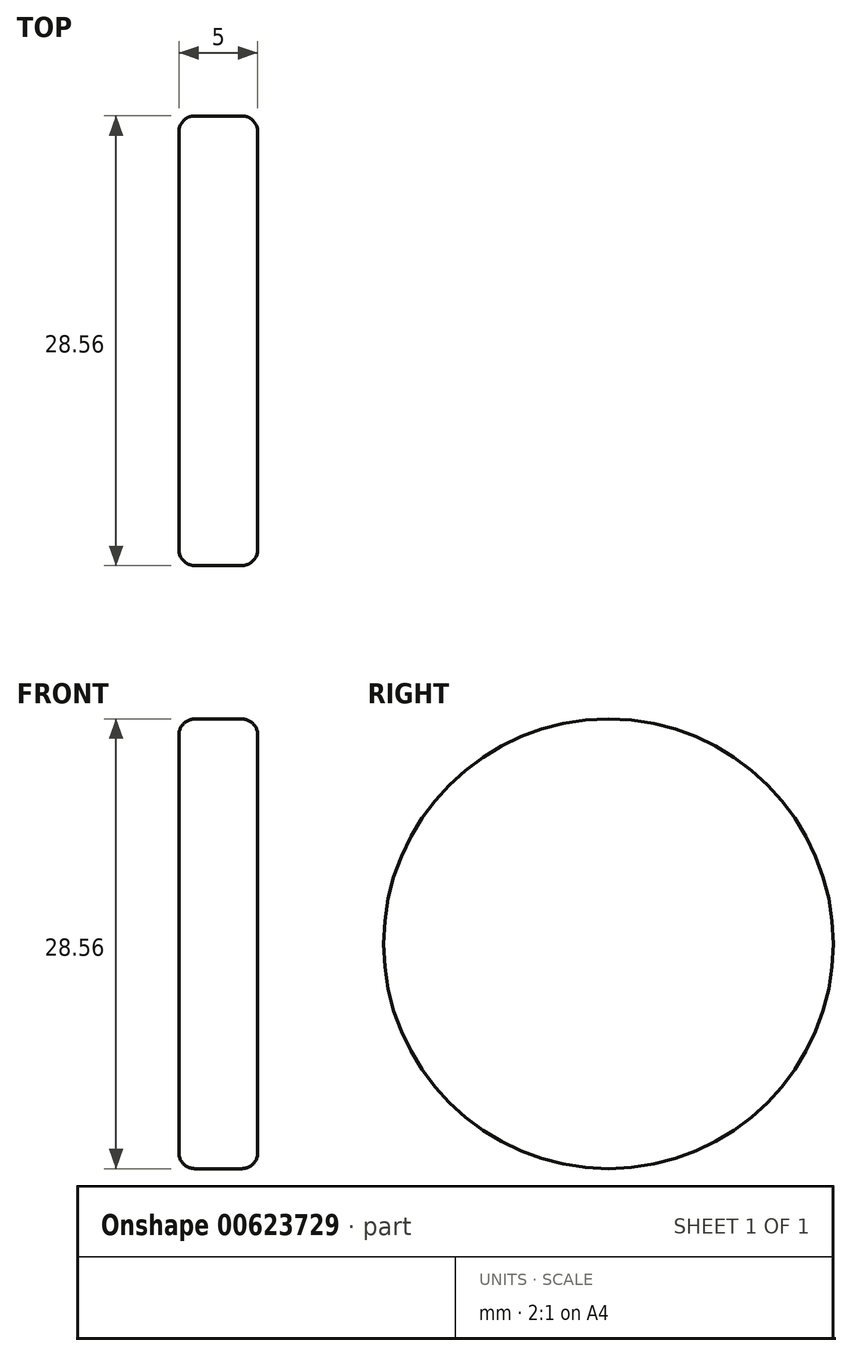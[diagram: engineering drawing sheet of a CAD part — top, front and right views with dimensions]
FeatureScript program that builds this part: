
annotation { "Feature Type Name" : "Feature", "Feature Type Description" : "" }
export const myFeature = defineFeature(function(context is Context, id is Id, definition is map)
    precondition{}
    {
        {
            var Q0;
            Q0=qCreatedBy(makeId("Right.planeOp"),FACE);
            var sketch = newSketch(context, id + "F0", { "sketchPlane" : qUnion([Q0])});
            skCircle(sketch, "E0", {"center": v(0, 0) * mm, "radius": 14.28 * mm});
            skSolve(sketch);
        }
        {
            var Q0;
            Q0 = qSketchRegion(id + "F0", true);
            extrude(context, id + "F1", {"entities" : qUnion([Q0]), "depth" : 5 * mm, "offsetDistance" : 25 * mm});
        }
        {
            var Q0;
            Q0=makeQuery(id+"F1.opExtrude","CAP_FACE",FACE,{"disambiguationData":[OSD([sQuery(id+"F0.wireOp",EDGE,"E0")])],"isStart":true});
            var Q1;
            Q1=makeQuery(id+"F1.opExtrude","CAP_EDGE",EDGE,{"disambiguationData":[OSD([sQuery(id+"F0.wireOp",EDGE,"E0")])],"isStart":false});
            var Q2;
            Q2=makeQuery(id+"F1.opExtrude","CAP_EDGE",EDGE,{"disambiguationData":[OSD([sQuery(id+"F0.wireOp",EDGE,"E0")])],"isStart":true});
            fillet(context, id + "F2", {"entities" : qUnion([Q0, Q1, Q2]), "radius" : 1 * mm, "tangentPropagation" : true, "allowEdgeOverflow" : false});
        }
    });
